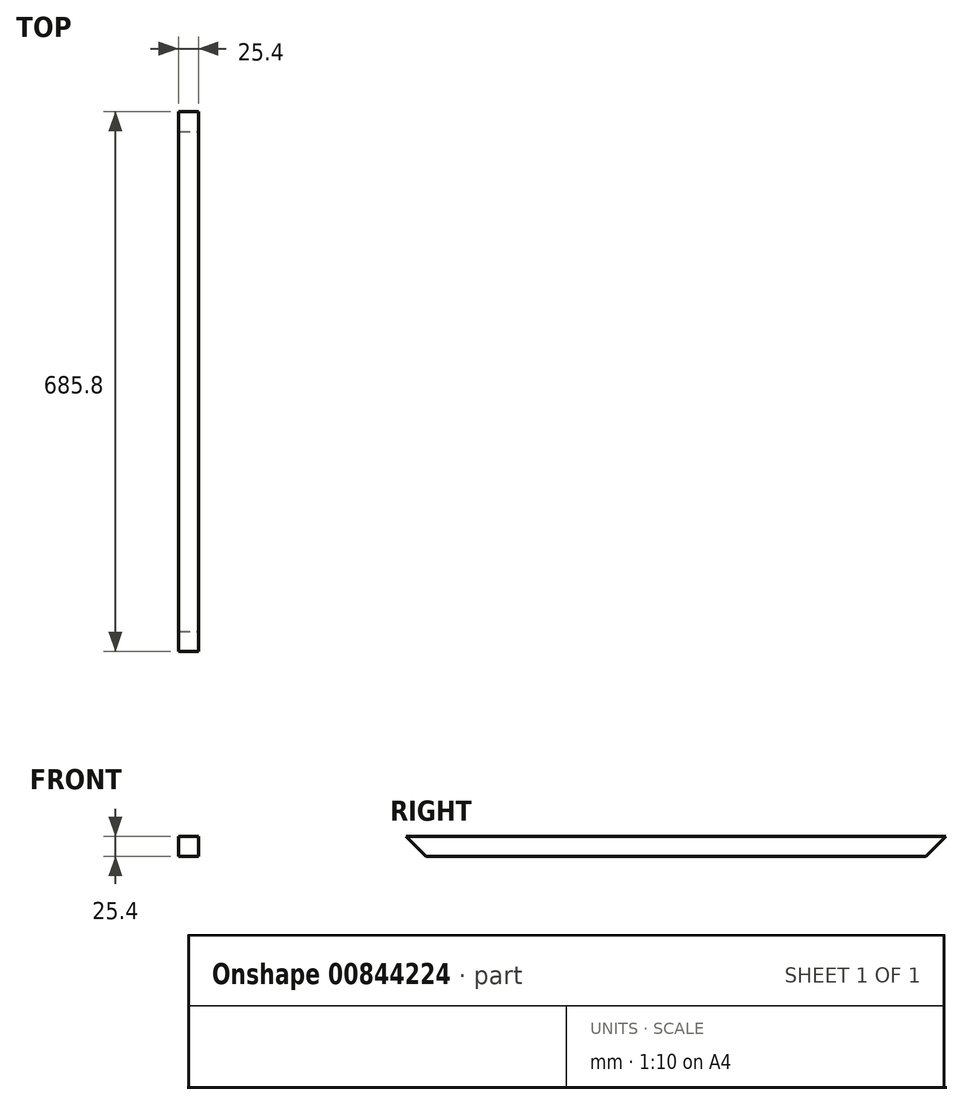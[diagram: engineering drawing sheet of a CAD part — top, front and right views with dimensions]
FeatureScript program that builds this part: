
annotation { "Feature Type Name" : "Feature", "Feature Type Description" : "" }
export const myFeature = defineFeature(function(context is Context, id is Id, definition is map)
    precondition{}
    {
        {
            var Q0;
            Q0=qCreatedBy(makeId("Front.planeOp"),FACE);
            var sketch = newSketch(context, id + "F0", { "sketchPlane" : qUnion([Q0])});
            skLineSegment(sketch, "E0.bottom", {"start": v(12.7, 12.7) * mm, "end": v(-12.7, 12.7) * mm});
            skLineSegment(sketch, "E0.top", {"start": v(12.7, -12.7) * mm, "end": v(-12.7, -12.7) * mm});
            skLineSegment(sketch, "E0.left", {"start": v(12.7, 12.7) * mm, "end": v(12.7, -12.7) * mm});
            skLineSegment(sketch, "E0.right", {"start": v(-12.7, 12.7) * mm, "end": v(-12.7, -12.7) * mm});
            skPoint(sketch, "E0.middle", {"position": v(0, 0) * mm});
            skSolve(sketch);
        }
        {
            var Q0;
            Q0 = qSketchRegion(id + "F0", true);
            extrude(context, id + "F1", {"entities" : qUnion([Q0]), "depth" : 685.8 * mm, "offsetDistance" : 25.4 * mm});
        }
        {
            var Q0;
            Q0=makeQuery(id+"F1.opExtrude","SWEPT_FACE",FACE,{"disambiguationData":[OSD([sQuery(id+"F0.wireOp",EDGE,"E0.left")])]});
            var sketch = newSketch(context, id + "F2", { "sketchPlane" : qUnion([Q0])});
            skLineSegment(sketch, "E1", {"start": v(-685.8, 12.7) * mm, "end": v(-685.8, -12.7) * mm});
            skLineSegment(sketch, "E2", {"start": v(-685.8, -12.7) * mm, "end": v(-660.4, -12.7) * mm});
            skLineSegment(sketch, "E3", {"start": v(-660.4, -12.7) * mm, "end": v(-685.8, 12.7) * mm});
            skLineSegment(sketch, "E4", {"start": v(0, 12.7) * mm, "end": v(0, -12.7) * mm});
            skLineSegment(sketch, "E5", {"start": v(0, -12.7) * mm, "end": v(-25.4, -12.7) * mm});
            skLineSegment(sketch, "E6", {"start": v(-25.4, -12.7) * mm, "end": v(0, 12.7) * mm});
            skSolve(sketch);
        }
        {
            var Q0;
            Q0 = qSketchRegion(id + "F2", true);
            extrude(context, id + "F3", {"entities" : qUnion([Q0]), "operationType" : NewBodyOperationType.REMOVE, "endBound" : BoundingType.THROUGH_ALL, "oppositeDirection" : true, "depth" : 25.4 * mm, "offsetDistance" : 25.4 * mm});
        }
    });
